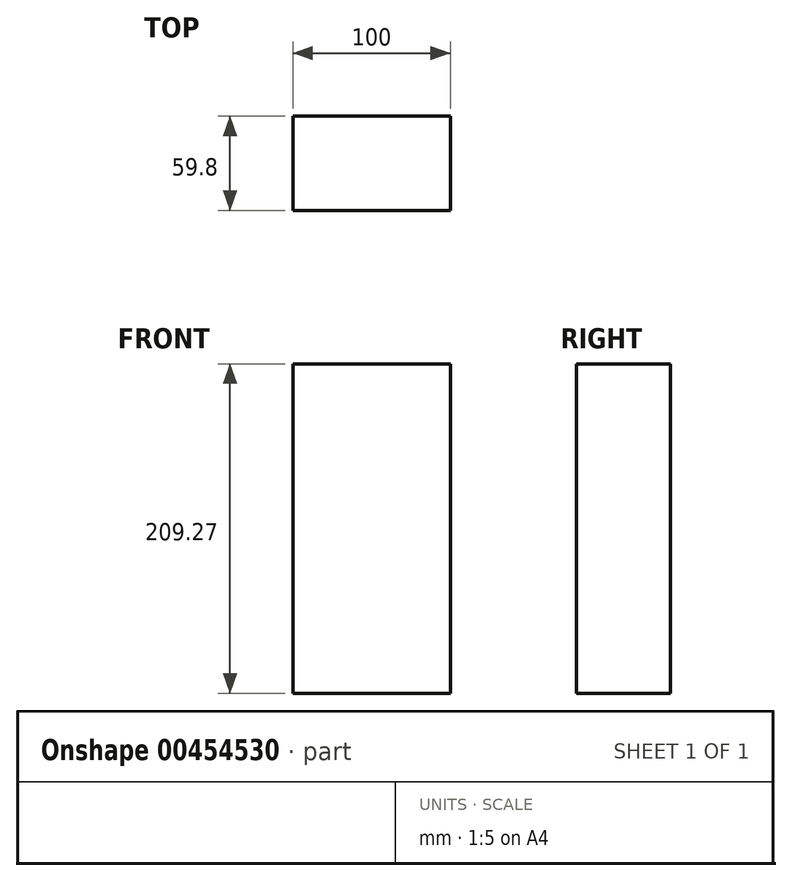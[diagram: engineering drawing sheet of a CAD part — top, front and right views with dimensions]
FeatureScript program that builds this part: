
annotation { "Feature Type Name" : "Feature", "Feature Type Description" : "" }
export const myFeature = defineFeature(function(context is Context, id is Id, definition is map)
    precondition{}
    {
        {
            var Q0;
            Q0=qCreatedBy(makeId("Top.planeOp"),FACE);
            var sketch = newSketch(context, id + "F0", { "sketchPlane" : qUnion([Q0])});
            skLineSegment(sketch, "E0.bottom", {"start": v(26.88, 71.47) * mm, "end": v(-513.12, 71.47) * mm});
            skLineSegment(sketch, "E0.top", {"start": v(26.88, -398.53) * mm, "end": v(-513.12, -398.53) * mm});
            skLineSegment(sketch, "E0.left", {"start": v(26.88, 71.47) * mm, "end": v(26.88, -398.53) * mm});
            skLineSegment(sketch, "E0.right", {"start": v(-513.12, 71.47) * mm, "end": v(-513.12, -398.53) * mm});
            skSolve(sketch);
        }
        {
            var Q0;
            Q0=makeQuery(id+"F0.imprint","IMPRINT",FACE,{"disambiguationData":[TD([[makeQuery(id+"F0.imprint","IMPRINT",EDGE,{"derivedFrom":sQuery(id+"F0.wireOp",EDGE,"E0.bottom")}),1.0]])]});
            var sketch = newSketch(context, id + "F1", { "sketchPlane" : qUnion([Q0])});
            skLineSegment(sketch, "E1.bottom", {"start": v(-360.12, -62.73) * mm, "end": v(-460.12, -62.73) * mm});
            skLineSegment(sketch, "E1.top", {"start": v(-360.12, -122.53) * mm, "end": v(-460.12, -122.53) * mm});
            skLineSegment(sketch, "E1.left", {"start": v(-360.12, -62.73) * mm, "end": v(-360.12, -122.53) * mm});
            skLineSegment(sketch, "E1.right", {"start": v(-460.12, -62.73) * mm, "end": v(-460.12, -122.53) * mm});
            skSolve(sketch);
        }
        {
            var Q0;
            Q0 = qSketchRegion(id + "F1", true);
            var Q1;
            Q1=sQuery(id+"F1.wireOp",EDGE,"E1.top");
            var Q2;
            Q2=sQuery(id+"F1.wireOp",EDGE,"E1.bottom");
            var Q3;
            Q3=sQuery(id+"F1.wireOp",EDGE,"E1.right");
            extrude(context, id + "F2", {"entities" : qUnion([Q0]), "surfaceEntities" : qUnion([Q1, Q2, Q3]), "depth" : 209.27 * mm});
        }
    });
